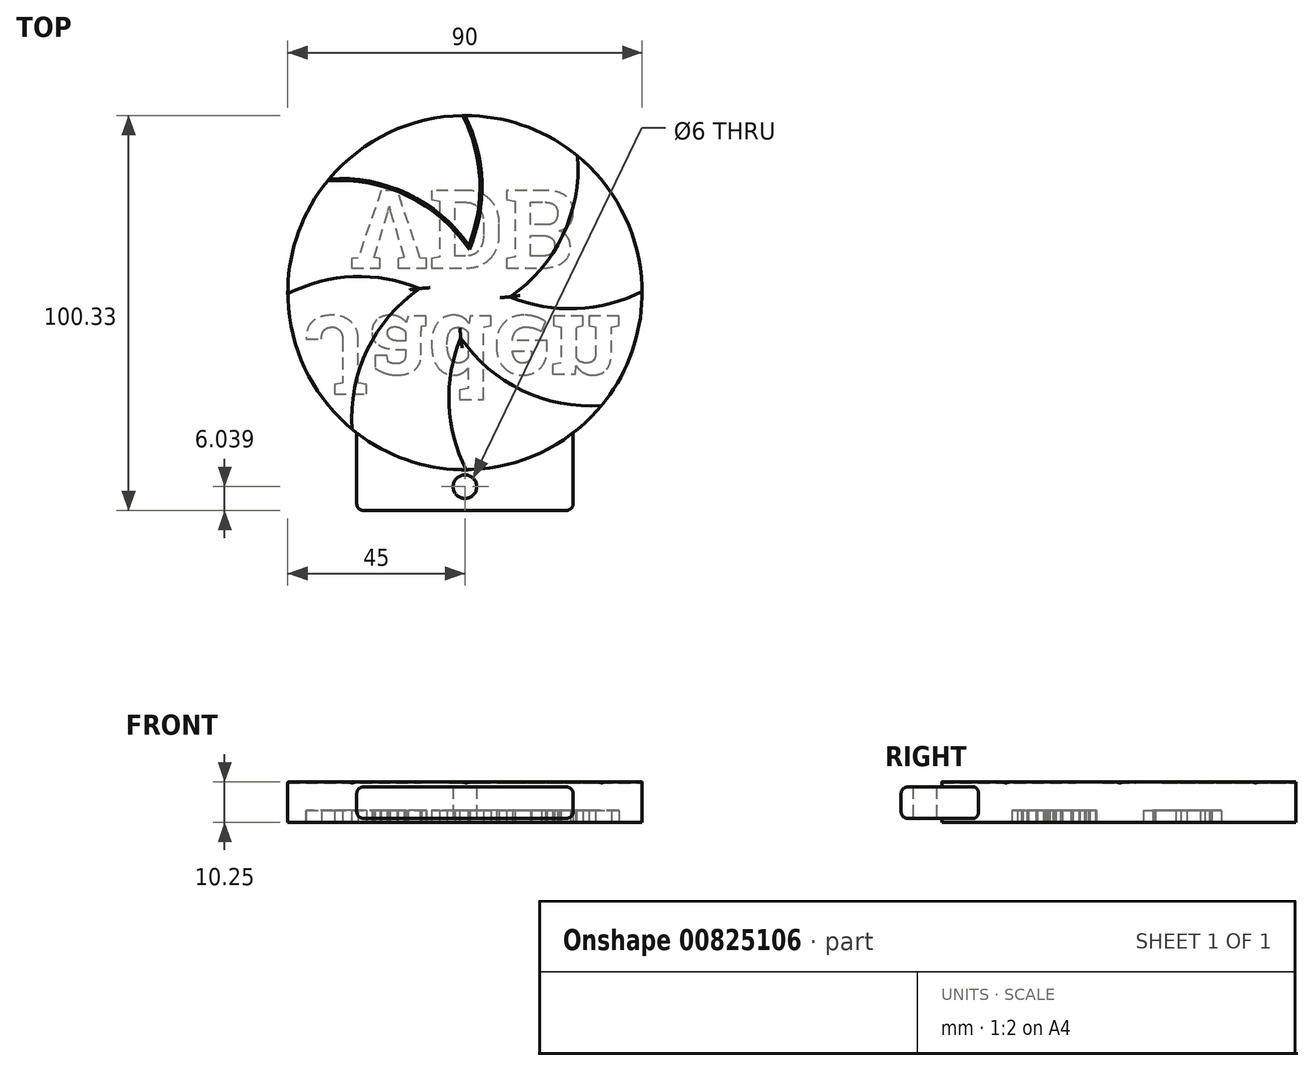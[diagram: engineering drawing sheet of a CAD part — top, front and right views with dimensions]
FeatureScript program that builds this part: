
annotation { "Feature Type Name" : "Feature", "Feature Type Description" : "" }
export const myFeature = defineFeature(function(context is Context, id is Id, definition is map)
    precondition{}
    {
        {
            var Q0;
            Q0=qCreatedBy(makeId("Top.planeOp"),FACE);
            var sketch = newSketch(context, id + "F0", { "sketchPlane" : qUnion([Q0])});
            skPoint(sketch, "E0.middle", {"position": v(0, 0) * mm});
            skCircle(sketch, "E1", {"center": v(0, 0) * mm, "radius": 45 * mm});
            skSolve(sketch);
        }
        {
            var Q0;
            Q0 = qSketchRegion(id + "F0", true);
            extrude(context, id + "F1", {"entities" : qUnion([Q0]), "endBound" : BoundingType.SYMMETRIC, "depth" : 10 * mm, "offsetDistance" : 25 * mm});
        }
        {
            var Q0;
            Q0=qCreatedBy(makeId("Top.planeOp"),FACE);
            var sketch = newSketch(context, id + "F2", { "sketchPlane" : qUnion([Q0])});
            skCircle(sketch, "E2.0", {"center": v(0, 0) * mm, "radius": 45 * mm});
            skLineSegment(sketch, "E3", {"start": v(-27.5, -35.62) * mm, "end": v(-27.5, -55.33) * mm});
            skLineSegment(sketch, "E4", {"start": v(-27.5, -55.33) * mm, "end": v(27.5, -55.33) * mm});
            skLineSegment(sketch, "E5", {"start": v(27.5, -55.33) * mm, "end": v(27.5, -35.62) * mm});
            skSolve(sketch);
        }
        {
            var Q0;
            Q0 = qSketchRegion(id + "F2", true);
            extrude(context, id + "F3", {"entities" : qUnion([Q0]), "operationType" : NewBodyOperationType.ADD, "endBound" : BoundingType.SYMMETRIC, "depth" : 8 * mm, "offsetDistance" : 25 * mm});
        }
        {
            var Q0;
            Q0=makeQuery(id+"F1.opExtrude","CAP_FACE",FACE,{"disambiguationData":[OSD([sQuery(id+"F0.wireOp",EDGE,"E1")])],"isStart":false});
            var sketch = newSketch(context, id + "F4", { "sketchPlane" : qUnion([Q0])});
            skArc(sketch, "E6", {"start": v(1, 12) * mm, "mid": v(-14.52, 25.11) * mm, "end": v(-34.48, 28.92) * mm});
            skArc(sketch, "E7", {"start": v(1, 12) * mm, "mid": v(3.78, 28.66) * mm, "end": v(-0.56, 45) * mm});
            skPoint(sketch, "E8.center", {"position": v(0, 0) * mm});
            skArc(sketch, "E9.0", {"start": v(-0.56, 45) * mm, "mid": v(-19.27, 40.66) * mm, "end": v(-34.48, 28.92) * mm});
            skArc(sketch, "E10.0", {"start": v(1.1, 10.95) * mm, "mid": v(4.3, 28.1) * mm, "end": v(0, 45) * mm});
            skArc(sketch, "E10.1", {"start": v(1.1, 10.95) * mm, "mid": v(-14.53, 24.57) * mm, "end": v(-34.92, 28.39) * mm});
            skArc(sketch, "E11.1.0", {"start": v(-10.95, 1.1) * mm, "mid": v(-28.1, 4.3) * mm, "end": v(-45, 0) * mm});
            skArc(sketch, "E11.1.1", {"start": v(-12, 1) * mm, "mid": v(-28.66, 3.78) * mm, "end": v(-45, -0.56) * mm});
            skArc(sketch, "E11.1.2", {"start": v(-12, 1) * mm, "mid": v(-25.11, -14.52) * mm, "end": v(-28.92, -34.48) * mm});
            skArc(sketch, "E11.1.3", {"start": v(-10.95, 1.1) * mm, "mid": v(-24.57, -14.53) * mm, "end": v(-28.39, -34.92) * mm});
            skArc(sketch, "E11.2.0", {"start": v(-1.1, -10.95) * mm, "mid": v(-4.3, -28.1) * mm, "end": v(0, -45) * mm});
            skArc(sketch, "E11.2.1", {"start": v(-1, -12) * mm, "mid": v(-3.78, -28.66) * mm, "end": v(0.56, -45) * mm});
            skArc(sketch, "E11.2.2", {"start": v(-1, -12) * mm, "mid": v(14.52, -25.11) * mm, "end": v(34.48, -28.92) * mm});
            skArc(sketch, "E11.2.3", {"start": v(-1.1, -10.95) * mm, "mid": v(14.53, -24.57) * mm, "end": v(34.92, -28.39) * mm});
            skArc(sketch, "E11.3.0", {"start": v(10.95, -1.1) * mm, "mid": v(28.1, -4.3) * mm, "end": v(45, 0) * mm});
            skArc(sketch, "E11.3.1", {"start": v(12, -1) * mm, "mid": v(28.66, -3.78) * mm, "end": v(45, 0.56) * mm});
            skArc(sketch, "E11.3.2", {"start": v(12, -1) * mm, "mid": v(25.11, 14.52) * mm, "end": v(28.92, 34.48) * mm});
            skArc(sketch, "E11.3.3", {"start": v(10.95, -1.1) * mm, "mid": v(24.57, 14.53) * mm, "end": v(28.39, 34.92) * mm});
            skArc(sketch, "E12.trimOffspring", {"start": v(-34.92, 28.39) * mm, "mid": v(-42.4, 15.06) * mm, "end": v(-45, 0) * mm});
            skArc(sketch, "E13.trimOffspring", {"start": v(-45, -0.56) * mm, "mid": v(-40.66, -19.27) * mm, "end": v(-28.92, -34.48) * mm});
            skArc(sketch, "E14.trimOffspring", {"start": v(-28.39, -34.92) * mm, "mid": v(-15.06, -42.4) * mm, "end": v(0, -45) * mm});
            skArc(sketch, "E15.trimOffspring", {"start": v(0.56, -45) * mm, "mid": v(19.27, -40.66) * mm, "end": v(34.48, -28.92) * mm});
            skArc(sketch, "E16.trimOffspring", {"start": v(34.92, -28.39) * mm, "mid": v(42.4, -15.06) * mm, "end": v(45, 0) * mm});
            skArc(sketch, "E17.trimOffspring", {"start": v(45, 0.56) * mm, "mid": v(40.66, 19.27) * mm, "end": v(28.92, 34.48) * mm});
            skArc(sketch, "E18.trimOffspring", {"start": v(28.39, 34.92) * mm, "mid": v(15.06, 42.4) * mm, "end": v(0, 45) * mm});
            skSolve(sketch);
        }
        {
            var Q0;
            Q0 = qSketchRegion(id + "F4", true);
            extrude(context, id + "F5", {"entities" : qUnion([Q0]), "operationType" : NewBodyOperationType.ADD, "depth" : .25 * mm, "offsetDistance" : 25 * mm});
        }
        {
            var Q0;
            Q0=makeQuery(id+"F5.opExtrude","CAP_EDGE",EDGE,{"disambiguationData":[OSD([sQuery(id+"F4.wireOp",EDGE,"E11.1.2")])],"isStart":true});
            var Q1;
            Q1=makeQuery(id+"F5.opExtrude","CAP_EDGE",EDGE,{"disambiguationData":[OSD([sQuery(id+"F4.wireOp",EDGE,"E11.1.3")])],"isStart":true});
            var Q2;
            Q2=makeQuery(id+"F5.opExtrude","CAP_EDGE",EDGE,{"disambiguationData":[OSD([sQuery(id+"F4.wireOp",EDGE,"E11.1.0")])],"isStart":true});
            var Q3;
            Q3=makeQuery(id+"F5.opExtrude","CAP_EDGE",EDGE,{"disambiguationData":[OSD([sQuery(id+"F4.wireOp",EDGE,"E11.1.1")])],"isStart":true});
            var Q4;
            Q4=makeQuery(id+"F5.opExtrude","CAP_EDGE",EDGE,{"disambiguationData":[OSD([sQuery(id+"F4.wireOp",EDGE,"E6")])],"isStart":true});
            var Q5;
            Q5=makeQuery(id+"F5.opExtrude","CAP_EDGE",EDGE,{"disambiguationData":[OSD([sQuery(id+"F4.wireOp",EDGE,"E10.1")])],"isStart":true});
            var Q6;
            Q6=makeQuery(id+"F5.opExtrude","CAP_EDGE",EDGE,{"disambiguationData":[OSD([sQuery(id+"F4.wireOp",EDGE,"E7")])],"isStart":true});
            var Q7;
            Q7=makeQuery(id+"F5.opExtrude","CAP_EDGE",EDGE,{"disambiguationData":[OSD([sQuery(id+"F4.wireOp",EDGE,"E10.0")])],"isStart":true});
            var Q8;
            Q8=makeQuery(id+"F5.opExtrude","CAP_EDGE",EDGE,{"disambiguationData":[OSD([sQuery(id+"F4.wireOp",EDGE,"E11.3.2")])],"isStart":true});
            var Q9;
            Q9=makeQuery(id+"F5.opExtrude","CAP_EDGE",EDGE,{"disambiguationData":[OSD([sQuery(id+"F4.wireOp",EDGE,"E11.3.3")])],"isStart":true});
            var Q10;
            Q10=makeQuery(id+"F5.opExtrude","CAP_EDGE",EDGE,{"disambiguationData":[OSD([sQuery(id+"F4.wireOp",EDGE,"E11.3.1")])],"isStart":true});
            var Q11;
            Q11=makeQuery(id+"F5.opExtrude","CAP_EDGE",EDGE,{"disambiguationData":[OSD([sQuery(id+"F4.wireOp",EDGE,"E11.3.0")])],"isStart":true});
            var Q12;
            Q12=makeQuery(id+"F5.opExtrude","CAP_EDGE",EDGE,{"disambiguationData":[OSD([sQuery(id+"F4.wireOp",EDGE,"E11.2.2")])],"isStart":true});
            var Q13;
            Q13=makeQuery(id+"F5.opExtrude","CAP_EDGE",EDGE,{"disambiguationData":[OSD([sQuery(id+"F4.wireOp",EDGE,"E11.2.3")])],"isStart":true});
            var Q14;
            Q14=makeQuery(id+"F5.opExtrude","CAP_EDGE",EDGE,{"disambiguationData":[OSD([sQuery(id+"F4.wireOp",EDGE,"E11.2.0")])],"isStart":true});
            var Q15;
            Q15=makeQuery(id+"F5.opExtrude","CAP_EDGE",EDGE,{"disambiguationData":[OSD([sQuery(id+"F4.wireOp",EDGE,"E11.2.1")])],"isStart":true});
            fillet(context, id + "F6", {"entities" : qUnion([Q0, Q1, Q2, Q3, Q4, Q5, Q6, Q7, Q8, Q9, Q10, Q11, Q12, Q13, Q14, Q15]), "radius" : .3 * mm, "tangentPropagation" : true, "allowEdgeOverflow" : false});
        }
        {
            var Q0;
            {var subQ0=sQuery(id+"F4.wireOp",EDGE,"E7");Q0=makeQuery(id+"F6.opFillet","BLEND_EDGE",EDGE,{"blendedFrom":[makeQuery(id+"F5.opExtrude","CAP_EDGE",EDGE,{"disambiguationData":[OSD([subQ0])],"isStart":true}),makeQuery(id+"F5.opExtrude","CAP_FACE",FACE,{"disambiguationData":[OSD([sQuery(id+"F4.wireOp",EDGE,"E6"),subQ0,sQuery(id+"F4.wireOp",EDGE,"E9.0")])],"isStart":false})],"blendedInto":[makeQuery(id+"F5.opExtrude","CAP_FACE",FACE,{"disambiguationData":[OSD([sQuery(id+"F4.wireOp",EDGE,"E6"),subQ0,sQuery(id+"F4.wireOp",EDGE,"E9.0")])],"isStart":false})]});}
            var Q1;
            {var subQ0=sQuery(id+"F4.wireOp",EDGE,"E10.0");Q1=makeQuery(id+"F6.opFillet","BLEND_EDGE",EDGE,{"blendedFrom":[makeQuery(id+"F5.opExtrude","CAP_EDGE",EDGE,{"disambiguationData":[OSD([subQ0])],"isStart":true}),makeQuery(id+"F5.opExtrude","CAP_FACE",FACE,{"disambiguationData":[OSD([subQ0,sQuery(id+"F4.wireOp",EDGE,"E10.1"),sQuery(id+"F4.wireOp",EDGE,"E11.1.0"),sQuery(id+"F4.wireOp",EDGE,"E11.1.3"),sQuery(id+"F4.wireOp",EDGE,"E11.2.0"),sQuery(id+"F4.wireOp",EDGE,"E11.2.3"),sQuery(id+"F4.wireOp",EDGE,"E11.3.0"),sQuery(id+"F4.wireOp",EDGE,"E11.3.3"),sQuery(id+"F4.wireOp",EDGE,"E12.trimOffspring"),sQuery(id+"F4.wireOp",EDGE,"E14.trimOffspring"),sQuery(id+"F4.wireOp",EDGE,"E16.trimOffspring"),sQuery(id+"F4.wireOp",EDGE,"E18.trimOffspring")])],"isStart":false})],"blendedInto":[makeQuery(id+"F5.opExtrude","CAP_FACE",FACE,{"disambiguationData":[OSD([subQ0,sQuery(id+"F4.wireOp",EDGE,"E10.1"),sQuery(id+"F4.wireOp",EDGE,"E11.1.0"),sQuery(id+"F4.wireOp",EDGE,"E11.1.3"),sQuery(id+"F4.wireOp",EDGE,"E11.2.0"),sQuery(id+"F4.wireOp",EDGE,"E11.2.3"),sQuery(id+"F4.wireOp",EDGE,"E11.3.0"),sQuery(id+"F4.wireOp",EDGE,"E11.3.3"),sQuery(id+"F4.wireOp",EDGE,"E12.trimOffspring"),sQuery(id+"F4.wireOp",EDGE,"E14.trimOffspring"),sQuery(id+"F4.wireOp",EDGE,"E16.trimOffspring"),sQuery(id+"F4.wireOp",EDGE,"E18.trimOffspring")])],"isStart":false})]});}
            var Q2;
            {var subQ0=sQuery(id+"F4.wireOp",EDGE,"E6");Q2=makeQuery(id+"F6.opFillet","BLEND_EDGE",EDGE,{"blendedFrom":[makeQuery(id+"F5.opExtrude","CAP_EDGE",EDGE,{"disambiguationData":[OSD([subQ0])],"isStart":true}),makeQuery(id+"F5.opExtrude","CAP_FACE",FACE,{"disambiguationData":[OSD([subQ0,sQuery(id+"F4.wireOp",EDGE,"E7"),sQuery(id+"F4.wireOp",EDGE,"E9.0")])],"isStart":false})],"blendedInto":[makeQuery(id+"F5.opExtrude","CAP_FACE",FACE,{"disambiguationData":[OSD([subQ0,sQuery(id+"F4.wireOp",EDGE,"E7"),sQuery(id+"F4.wireOp",EDGE,"E9.0")])],"isStart":false})]});}
            var Q3;
            {var subQ0=sQuery(id+"F4.wireOp",EDGE,"E10.1");Q3=makeQuery(id+"F6.opFillet","BLEND_EDGE",EDGE,{"blendedFrom":[makeQuery(id+"F5.opExtrude","CAP_EDGE",EDGE,{"disambiguationData":[OSD([subQ0])],"isStart":true}),makeQuery(id+"F5.opExtrude","CAP_FACE",FACE,{"disambiguationData":[OSD([sQuery(id+"F4.wireOp",EDGE,"E10.0"),subQ0,sQuery(id+"F4.wireOp",EDGE,"E11.1.0"),sQuery(id+"F4.wireOp",EDGE,"E11.1.3"),sQuery(id+"F4.wireOp",EDGE,"E11.2.0"),sQuery(id+"F4.wireOp",EDGE,"E11.2.3"),sQuery(id+"F4.wireOp",EDGE,"E11.3.0"),sQuery(id+"F4.wireOp",EDGE,"E11.3.3"),sQuery(id+"F4.wireOp",EDGE,"E12.trimOffspring"),sQuery(id+"F4.wireOp",EDGE,"E14.trimOffspring"),sQuery(id+"F4.wireOp",EDGE,"E16.trimOffspring"),sQuery(id+"F4.wireOp",EDGE,"E18.trimOffspring")])],"isStart":false})],"blendedInto":[makeQuery(id+"F5.opExtrude","CAP_FACE",FACE,{"disambiguationData":[OSD([sQuery(id+"F4.wireOp",EDGE,"E10.0"),subQ0,sQuery(id+"F4.wireOp",EDGE,"E11.1.0"),sQuery(id+"F4.wireOp",EDGE,"E11.1.3"),sQuery(id+"F4.wireOp",EDGE,"E11.2.0"),sQuery(id+"F4.wireOp",EDGE,"E11.2.3"),sQuery(id+"F4.wireOp",EDGE,"E11.3.0"),sQuery(id+"F4.wireOp",EDGE,"E11.3.3"),sQuery(id+"F4.wireOp",EDGE,"E12.trimOffspring"),sQuery(id+"F4.wireOp",EDGE,"E14.trimOffspring"),sQuery(id+"F4.wireOp",EDGE,"E16.trimOffspring"),sQuery(id+"F4.wireOp",EDGE,"E18.trimOffspring")])],"isStart":false})]});}
            var Q4;
            {var subQ0=sQuery(id+"F4.wireOp",EDGE,"E11.3.3");Q4=makeQuery(id+"F6.opFillet","BLEND_EDGE",EDGE,{"blendedFrom":[makeQuery(id+"F5.opExtrude","CAP_EDGE",EDGE,{"disambiguationData":[OSD([subQ0])],"isStart":true}),makeQuery(id+"F5.opExtrude","CAP_FACE",FACE,{"disambiguationData":[OSD([sQuery(id+"F4.wireOp",EDGE,"E10.0"),sQuery(id+"F4.wireOp",EDGE,"E10.1"),sQuery(id+"F4.wireOp",EDGE,"E11.1.0"),sQuery(id+"F4.wireOp",EDGE,"E11.1.3"),sQuery(id+"F4.wireOp",EDGE,"E11.2.0"),sQuery(id+"F4.wireOp",EDGE,"E11.2.3"),sQuery(id+"F4.wireOp",EDGE,"E11.3.0"),subQ0,sQuery(id+"F4.wireOp",EDGE,"E12.trimOffspring"),sQuery(id+"F4.wireOp",EDGE,"E14.trimOffspring"),sQuery(id+"F4.wireOp",EDGE,"E16.trimOffspring"),sQuery(id+"F4.wireOp",EDGE,"E18.trimOffspring")])],"isStart":false})],"blendedInto":[makeQuery(id+"F5.opExtrude","CAP_FACE",FACE,{"disambiguationData":[OSD([sQuery(id+"F4.wireOp",EDGE,"E10.0"),sQuery(id+"F4.wireOp",EDGE,"E10.1"),sQuery(id+"F4.wireOp",EDGE,"E11.1.0"),sQuery(id+"F4.wireOp",EDGE,"E11.1.3"),sQuery(id+"F4.wireOp",EDGE,"E11.2.0"),sQuery(id+"F4.wireOp",EDGE,"E11.2.3"),sQuery(id+"F4.wireOp",EDGE,"E11.3.0"),subQ0,sQuery(id+"F4.wireOp",EDGE,"E12.trimOffspring"),sQuery(id+"F4.wireOp",EDGE,"E14.trimOffspring"),sQuery(id+"F4.wireOp",EDGE,"E16.trimOffspring"),sQuery(id+"F4.wireOp",EDGE,"E18.trimOffspring")])],"isStart":false})]});}
            var Q5;
            {var subQ0=sQuery(id+"F4.wireOp",EDGE,"E11.3.2");Q5=makeQuery(id+"F6.opFillet","BLEND_EDGE",EDGE,{"blendedFrom":[makeQuery(id+"F5.opExtrude","CAP_EDGE",EDGE,{"disambiguationData":[OSD([subQ0])],"isStart":true}),makeQuery(id+"F5.opExtrude","CAP_FACE",FACE,{"disambiguationData":[OSD([sQuery(id+"F4.wireOp",EDGE,"E11.3.1"),subQ0,sQuery(id+"F4.wireOp",EDGE,"E17.trimOffspring")])],"isStart":false})],"blendedInto":[makeQuery(id+"F5.opExtrude","CAP_FACE",FACE,{"disambiguationData":[OSD([sQuery(id+"F4.wireOp",EDGE,"E11.3.1"),subQ0,sQuery(id+"F4.wireOp",EDGE,"E17.trimOffspring")])],"isStart":false})]});}
            var Q6;
            {var subQ0=sQuery(id+"F4.wireOp",EDGE,"E11.3.1");Q6=makeQuery(id+"F6.opFillet","BLEND_EDGE",EDGE,{"blendedFrom":[makeQuery(id+"F5.opExtrude","CAP_EDGE",EDGE,{"disambiguationData":[OSD([subQ0])],"isStart":true}),makeQuery(id+"F5.opExtrude","CAP_FACE",FACE,{"disambiguationData":[OSD([subQ0,sQuery(id+"F4.wireOp",EDGE,"E11.3.2"),sQuery(id+"F4.wireOp",EDGE,"E17.trimOffspring")])],"isStart":false})],"blendedInto":[makeQuery(id+"F5.opExtrude","CAP_FACE",FACE,{"disambiguationData":[OSD([subQ0,sQuery(id+"F4.wireOp",EDGE,"E11.3.2"),sQuery(id+"F4.wireOp",EDGE,"E17.trimOffspring")])],"isStart":false})]});}
            var Q7;
            {var subQ0=sQuery(id+"F4.wireOp",EDGE,"E11.3.0");Q7=makeQuery(id+"F6.opFillet","BLEND_EDGE",EDGE,{"blendedFrom":[makeQuery(id+"F5.opExtrude","CAP_EDGE",EDGE,{"disambiguationData":[OSD([subQ0])],"isStart":true}),makeQuery(id+"F5.opExtrude","CAP_FACE",FACE,{"disambiguationData":[OSD([sQuery(id+"F4.wireOp",EDGE,"E10.0"),sQuery(id+"F4.wireOp",EDGE,"E10.1"),sQuery(id+"F4.wireOp",EDGE,"E11.1.0"),sQuery(id+"F4.wireOp",EDGE,"E11.1.3"),sQuery(id+"F4.wireOp",EDGE,"E11.2.0"),sQuery(id+"F4.wireOp",EDGE,"E11.2.3"),subQ0,sQuery(id+"F4.wireOp",EDGE,"E11.3.3"),sQuery(id+"F4.wireOp",EDGE,"E12.trimOffspring"),sQuery(id+"F4.wireOp",EDGE,"E14.trimOffspring"),sQuery(id+"F4.wireOp",EDGE,"E16.trimOffspring"),sQuery(id+"F4.wireOp",EDGE,"E18.trimOffspring")])],"isStart":false})],"blendedInto":[makeQuery(id+"F5.opExtrude","CAP_FACE",FACE,{"disambiguationData":[OSD([sQuery(id+"F4.wireOp",EDGE,"E10.0"),sQuery(id+"F4.wireOp",EDGE,"E10.1"),sQuery(id+"F4.wireOp",EDGE,"E11.1.0"),sQuery(id+"F4.wireOp",EDGE,"E11.1.3"),sQuery(id+"F4.wireOp",EDGE,"E11.2.0"),sQuery(id+"F4.wireOp",EDGE,"E11.2.3"),subQ0,sQuery(id+"F4.wireOp",EDGE,"E11.3.3"),sQuery(id+"F4.wireOp",EDGE,"E12.trimOffspring"),sQuery(id+"F4.wireOp",EDGE,"E14.trimOffspring"),sQuery(id+"F4.wireOp",EDGE,"E16.trimOffspring"),sQuery(id+"F4.wireOp",EDGE,"E18.trimOffspring")])],"isStart":false})]});}
            var Q8;
            {var subQ0=sQuery(id+"F4.wireOp",EDGE,"E11.2.3");Q8=makeQuery(id+"F6.opFillet","BLEND_EDGE",EDGE,{"blendedFrom":[makeQuery(id+"F5.opExtrude","CAP_EDGE",EDGE,{"disambiguationData":[OSD([subQ0])],"isStart":true}),makeQuery(id+"F5.opExtrude","CAP_FACE",FACE,{"disambiguationData":[OSD([sQuery(id+"F4.wireOp",EDGE,"E10.0"),sQuery(id+"F4.wireOp",EDGE,"E10.1"),sQuery(id+"F4.wireOp",EDGE,"E11.1.0"),sQuery(id+"F4.wireOp",EDGE,"E11.1.3"),sQuery(id+"F4.wireOp",EDGE,"E11.2.0"),subQ0,sQuery(id+"F4.wireOp",EDGE,"E11.3.0"),sQuery(id+"F4.wireOp",EDGE,"E11.3.3"),sQuery(id+"F4.wireOp",EDGE,"E12.trimOffspring"),sQuery(id+"F4.wireOp",EDGE,"E14.trimOffspring"),sQuery(id+"F4.wireOp",EDGE,"E16.trimOffspring"),sQuery(id+"F4.wireOp",EDGE,"E18.trimOffspring")])],"isStart":false})],"blendedInto":[makeQuery(id+"F5.opExtrude","CAP_FACE",FACE,{"disambiguationData":[OSD([sQuery(id+"F4.wireOp",EDGE,"E10.0"),sQuery(id+"F4.wireOp",EDGE,"E10.1"),sQuery(id+"F4.wireOp",EDGE,"E11.1.0"),sQuery(id+"F4.wireOp",EDGE,"E11.1.3"),sQuery(id+"F4.wireOp",EDGE,"E11.2.0"),subQ0,sQuery(id+"F4.wireOp",EDGE,"E11.3.0"),sQuery(id+"F4.wireOp",EDGE,"E11.3.3"),sQuery(id+"F4.wireOp",EDGE,"E12.trimOffspring"),sQuery(id+"F4.wireOp",EDGE,"E14.trimOffspring"),sQuery(id+"F4.wireOp",EDGE,"E16.trimOffspring"),sQuery(id+"F4.wireOp",EDGE,"E18.trimOffspring")])],"isStart":false})]});}
            var Q9;
            {var subQ0=sQuery(id+"F4.wireOp",EDGE,"E11.2.2");Q9=makeQuery(id+"F6.opFillet","BLEND_EDGE",EDGE,{"blendedFrom":[makeQuery(id+"F5.opExtrude","CAP_EDGE",EDGE,{"disambiguationData":[OSD([subQ0])],"isStart":true}),makeQuery(id+"F5.opExtrude","CAP_FACE",FACE,{"disambiguationData":[OSD([sQuery(id+"F4.wireOp",EDGE,"E11.2.1"),subQ0,sQuery(id+"F4.wireOp",EDGE,"E15.trimOffspring")])],"isStart":false})],"blendedInto":[makeQuery(id+"F5.opExtrude","CAP_FACE",FACE,{"disambiguationData":[OSD([sQuery(id+"F4.wireOp",EDGE,"E11.2.1"),subQ0,sQuery(id+"F4.wireOp",EDGE,"E15.trimOffspring")])],"isStart":false})]});}
            var Q10;
            {var subQ0=sQuery(id+"F4.wireOp",EDGE,"E11.2.1");Q10=makeQuery(id+"F6.opFillet","BLEND_EDGE",EDGE,{"blendedFrom":[makeQuery(id+"F5.opExtrude","CAP_EDGE",EDGE,{"disambiguationData":[OSD([subQ0])],"isStart":true}),makeQuery(id+"F5.opExtrude","CAP_FACE",FACE,{"disambiguationData":[OSD([subQ0,sQuery(id+"F4.wireOp",EDGE,"E11.2.2"),sQuery(id+"F4.wireOp",EDGE,"E15.trimOffspring")])],"isStart":false})],"blendedInto":[makeQuery(id+"F5.opExtrude","CAP_FACE",FACE,{"disambiguationData":[OSD([subQ0,sQuery(id+"F4.wireOp",EDGE,"E11.2.2"),sQuery(id+"F4.wireOp",EDGE,"E15.trimOffspring")])],"isStart":false})]});}
            var Q11;
            {var subQ0=sQuery(id+"F4.wireOp",EDGE,"E11.2.0");Q11=makeQuery(id+"F6.opFillet","BLEND_EDGE",EDGE,{"blendedFrom":[makeQuery(id+"F5.opExtrude","CAP_EDGE",EDGE,{"disambiguationData":[OSD([subQ0])],"isStart":true}),makeQuery(id+"F5.opExtrude","CAP_FACE",FACE,{"disambiguationData":[OSD([sQuery(id+"F4.wireOp",EDGE,"E10.0"),sQuery(id+"F4.wireOp",EDGE,"E10.1"),sQuery(id+"F4.wireOp",EDGE,"E11.1.0"),sQuery(id+"F4.wireOp",EDGE,"E11.1.3"),subQ0,sQuery(id+"F4.wireOp",EDGE,"E11.2.3"),sQuery(id+"F4.wireOp",EDGE,"E11.3.0"),sQuery(id+"F4.wireOp",EDGE,"E11.3.3"),sQuery(id+"F4.wireOp",EDGE,"E12.trimOffspring"),sQuery(id+"F4.wireOp",EDGE,"E14.trimOffspring"),sQuery(id+"F4.wireOp",EDGE,"E16.trimOffspring"),sQuery(id+"F4.wireOp",EDGE,"E18.trimOffspring")])],"isStart":false})],"blendedInto":[makeQuery(id+"F5.opExtrude","CAP_FACE",FACE,{"disambiguationData":[OSD([sQuery(id+"F4.wireOp",EDGE,"E10.0"),sQuery(id+"F4.wireOp",EDGE,"E10.1"),sQuery(id+"F4.wireOp",EDGE,"E11.1.0"),sQuery(id+"F4.wireOp",EDGE,"E11.1.3"),subQ0,sQuery(id+"F4.wireOp",EDGE,"E11.2.3"),sQuery(id+"F4.wireOp",EDGE,"E11.3.0"),sQuery(id+"F4.wireOp",EDGE,"E11.3.3"),sQuery(id+"F4.wireOp",EDGE,"E12.trimOffspring"),sQuery(id+"F4.wireOp",EDGE,"E14.trimOffspring"),sQuery(id+"F4.wireOp",EDGE,"E16.trimOffspring"),sQuery(id+"F4.wireOp",EDGE,"E18.trimOffspring")])],"isStart":false})]});}
            var Q12;
            {var subQ0=sQuery(id+"F4.wireOp",EDGE,"E11.1.0");Q12=makeQuery(id+"F6.opFillet","BLEND_EDGE",EDGE,{"blendedFrom":[makeQuery(id+"F5.opExtrude","CAP_EDGE",EDGE,{"disambiguationData":[OSD([subQ0])],"isStart":true}),makeQuery(id+"F5.opExtrude","CAP_FACE",FACE,{"disambiguationData":[OSD([sQuery(id+"F4.wireOp",EDGE,"E10.0"),sQuery(id+"F4.wireOp",EDGE,"E10.1"),subQ0,sQuery(id+"F4.wireOp",EDGE,"E11.1.3"),sQuery(id+"F4.wireOp",EDGE,"E11.2.0"),sQuery(id+"F4.wireOp",EDGE,"E11.2.3"),sQuery(id+"F4.wireOp",EDGE,"E11.3.0"),sQuery(id+"F4.wireOp",EDGE,"E11.3.3"),sQuery(id+"F4.wireOp",EDGE,"E12.trimOffspring"),sQuery(id+"F4.wireOp",EDGE,"E14.trimOffspring"),sQuery(id+"F4.wireOp",EDGE,"E16.trimOffspring"),sQuery(id+"F4.wireOp",EDGE,"E18.trimOffspring")])],"isStart":false})],"blendedInto":[makeQuery(id+"F5.opExtrude","CAP_FACE",FACE,{"disambiguationData":[OSD([sQuery(id+"F4.wireOp",EDGE,"E10.0"),sQuery(id+"F4.wireOp",EDGE,"E10.1"),subQ0,sQuery(id+"F4.wireOp",EDGE,"E11.1.3"),sQuery(id+"F4.wireOp",EDGE,"E11.2.0"),sQuery(id+"F4.wireOp",EDGE,"E11.2.3"),sQuery(id+"F4.wireOp",EDGE,"E11.3.0"),sQuery(id+"F4.wireOp",EDGE,"E11.3.3"),sQuery(id+"F4.wireOp",EDGE,"E12.trimOffspring"),sQuery(id+"F4.wireOp",EDGE,"E14.trimOffspring"),sQuery(id+"F4.wireOp",EDGE,"E16.trimOffspring"),sQuery(id+"F4.wireOp",EDGE,"E18.trimOffspring")])],"isStart":false})]});}
            var Q13;
            {var subQ0=sQuery(id+"F4.wireOp",EDGE,"E11.1.1");Q13=makeQuery(id+"F6.opFillet","BLEND_EDGE",EDGE,{"blendedFrom":[makeQuery(id+"F5.opExtrude","CAP_EDGE",EDGE,{"disambiguationData":[OSD([subQ0])],"isStart":true}),makeQuery(id+"F5.opExtrude","CAP_FACE",FACE,{"disambiguationData":[OSD([subQ0,sQuery(id+"F4.wireOp",EDGE,"E11.1.2"),sQuery(id+"F4.wireOp",EDGE,"E13.trimOffspring")])],"isStart":false})],"blendedInto":[makeQuery(id+"F5.opExtrude","CAP_FACE",FACE,{"disambiguationData":[OSD([subQ0,sQuery(id+"F4.wireOp",EDGE,"E11.1.2"),sQuery(id+"F4.wireOp",EDGE,"E13.trimOffspring")])],"isStart":false})]});}
            var Q14;
            {var subQ0=sQuery(id+"F4.wireOp",EDGE,"E11.1.2");Q14=makeQuery(id+"F6.opFillet","BLEND_EDGE",EDGE,{"blendedFrom":[makeQuery(id+"F5.opExtrude","CAP_EDGE",EDGE,{"disambiguationData":[OSD([subQ0])],"isStart":true}),makeQuery(id+"F5.opExtrude","CAP_FACE",FACE,{"disambiguationData":[OSD([sQuery(id+"F4.wireOp",EDGE,"E11.1.1"),subQ0,sQuery(id+"F4.wireOp",EDGE,"E13.trimOffspring")])],"isStart":false})],"blendedInto":[makeQuery(id+"F5.opExtrude","CAP_FACE",FACE,{"disambiguationData":[OSD([sQuery(id+"F4.wireOp",EDGE,"E11.1.1"),subQ0,sQuery(id+"F4.wireOp",EDGE,"E13.trimOffspring")])],"isStart":false})]});}
            var Q15;
            {var subQ0=sQuery(id+"F4.wireOp",EDGE,"E11.1.3");Q15=makeQuery(id+"F6.opFillet","BLEND_EDGE",EDGE,{"blendedFrom":[makeQuery(id+"F5.opExtrude","CAP_EDGE",EDGE,{"disambiguationData":[OSD([subQ0])],"isStart":true}),makeQuery(id+"F5.opExtrude","CAP_FACE",FACE,{"disambiguationData":[OSD([sQuery(id+"F4.wireOp",EDGE,"E10.0"),sQuery(id+"F4.wireOp",EDGE,"E10.1"),sQuery(id+"F4.wireOp",EDGE,"E11.1.0"),subQ0,sQuery(id+"F4.wireOp",EDGE,"E11.2.0"),sQuery(id+"F4.wireOp",EDGE,"E11.2.3"),sQuery(id+"F4.wireOp",EDGE,"E11.3.0"),sQuery(id+"F4.wireOp",EDGE,"E11.3.3"),sQuery(id+"F4.wireOp",EDGE,"E12.trimOffspring"),sQuery(id+"F4.wireOp",EDGE,"E14.trimOffspring"),sQuery(id+"F4.wireOp",EDGE,"E16.trimOffspring"),sQuery(id+"F4.wireOp",EDGE,"E18.trimOffspring")])],"isStart":false})],"blendedInto":[makeQuery(id+"F5.opExtrude","CAP_FACE",FACE,{"disambiguationData":[OSD([sQuery(id+"F4.wireOp",EDGE,"E10.0"),sQuery(id+"F4.wireOp",EDGE,"E10.1"),sQuery(id+"F4.wireOp",EDGE,"E11.1.0"),subQ0,sQuery(id+"F4.wireOp",EDGE,"E11.2.0"),sQuery(id+"F4.wireOp",EDGE,"E11.2.3"),sQuery(id+"F4.wireOp",EDGE,"E11.3.0"),sQuery(id+"F4.wireOp",EDGE,"E11.3.3"),sQuery(id+"F4.wireOp",EDGE,"E12.trimOffspring"),sQuery(id+"F4.wireOp",EDGE,"E14.trimOffspring"),sQuery(id+"F4.wireOp",EDGE,"E16.trimOffspring"),sQuery(id+"F4.wireOp",EDGE,"E18.trimOffspring")])],"isStart":false})]});}
            fillet(context, id + "F7", {"entities" : qUnion([Q0, Q1, Q2, Q3, Q4, Q5, Q6, Q7, Q8, Q9, Q10, Q11, Q12, Q13, Q14, Q15]), "radius" : 3 * mm, "tangentPropagation" : true, "allowEdgeOverflow" : false});
        }
        {
            var Q0;
            Q0=makeQuery(id+"F1.opExtrude","CAP_FACE",FACE,{"disambiguationData":[OSD([sQuery(id+"F0.wireOp",EDGE,"E1")])],"isStart":true});
            var sketch = newSketch(context, id + "F8", { "sketchPlane" : qUnion([Q0])});
            skText(sketch, "E19", { "text": "Jaden\n", "fontName": "RobotoSlab-Bold.ttf"});
            const initialGuessF8  = {"E19": [-0.0408, 0.006, 1, 0, 0.02]};
            skSetInitialGuess(sketch, initialGuessF8);
            skSolve(sketch);
        }
        {
            var Q0;
            Q0=makeQuery(id+"F3.opExtrude","CAP_FACE",FACE,{"disambiguationData":[OSD([sQuery(id+"F2.wireOp",EDGE,"E2.0"),sQuery(id+"F2.wireOp",EDGE,"E3"),sQuery(id+"F2.wireOp",EDGE,"E4"),sQuery(id+"F2.wireOp",EDGE,"E5")])],"isStart":true});
            var sketch = newSketch(context, id + "F9", { "sketchPlane" : qUnion([Q0])});
            skPoint(sketch, "E20", {"position": v(0, 49.3) * mm});
            skSolve(sketch);
        }
        {
            var Q0;
            Q0=sQuery(id+"F9.wireOp",VERTEX,"E20");
            var Q1;
            Q1=makeQuery(id+"F1.opExtrude","SWEPT_BODY",BODY,{"disambiguationData":[OSD([sQuery(id+"F0.wireOp",EDGE,"E1")])]});
            hole(context, id + "F10", {"style" : HoleStyle.SIMPLE, "endStyle" : HoleEndStyle.THROUGH, "holeDiameter" : 6 * mm, "majorDiameter" : 5 * mm, "isTappedThrough" : true, "tappedDepth" : 12 * mm, "tapClearance" : 3, "locations" : qUnion([Q0]), "scope" : qUnion([Q1])});
        }
        {
            var Q0;
            Q0=makeQuery(id+"F8.imprint","IMPRINT",FACE,{"disambiguationData":[TD([[makeQuery(id+"F8.imprint","IMPRINT",EDGE,{"derivedFrom":sQuery(id+"F8.wireOp",EDGE,"E19.sketch_text.stroke-0")}),1.0]])]});
            var sketch = newSketch(context, id + "F11", { "sketchPlane" : qUnion([Q0])});
            skText(sketch, "E21", { "text": "VDB", "fontName": "RobotoSlab-Bold.ttf"});
            const initialGuessF11  = {"E21": [-0.0292, -0.026, 1, 0, 0.02]};
            skSetInitialGuess(sketch, initialGuessF11);
            skSolve(sketch);
        }
        {
            var Q0;
            Q0 = qSketchRegion(id + "F11", true);
            var Q1;
            Q1 = qSketchRegion(id + "F8", true);
            extrude(context, id + "F12", {"entities" : qUnion([Q0, Q1]), "operationType" : NewBodyOperationType.REMOVE, "oppositeDirection" : true, "depth" : 3 * mm, "offsetDistance" : 25 * mm});
        }
        {
            var Q0;
            Q0=makeQuery(id+"F3.opExtrude","CAP_EDGE",EDGE,{"disambiguationData":[OSD([sQuery(id+"F2.wireOp",EDGE,"E3")])],"isStart":true});
            var Q1;
            Q1=makeQuery(id+"F3.opExtrude","CAP_EDGE",EDGE,{"disambiguationData":[OSD([sQuery(id+"F2.wireOp",EDGE,"E3")])],"isStart":false});
            var Q2;
            Q2=makeQuery(id+"F3.opExtrude","CAP_EDGE",EDGE,{"disambiguationData":[OSD([sQuery(id+"F2.wireOp",EDGE,"E4")])],"isStart":false});
            var Q3;
            Q3=makeQuery(id+"F3.opExtrude","CAP_EDGE",EDGE,{"disambiguationData":[OSD([sQuery(id+"F2.wireOp",EDGE,"E4")])],"isStart":true});
            var Q4;
            Q4=makeQuery(id+"F3.opExtrude","SWEPT_EDGE",EDGE,{"disambiguationData":[OSD([sQuery(id+"F2.wireOp",EDGE,"E3"),sQuery(id+"F2.wireOp",EDGE,"E4")])]});
            var Q5;
            Q5=makeQuery(id+"F3.opExtrude","SWEPT_EDGE",EDGE,{"disambiguationData":[OSD([sQuery(id+"F2.wireOp",EDGE,"E4"),sQuery(id+"F2.wireOp",EDGE,"E5")])]});
            var Q6;
            Q6=makeQuery(id+"F3.opExtrude","CAP_EDGE",EDGE,{"disambiguationData":[OSD([sQuery(id+"F2.wireOp",EDGE,"E5")])],"isStart":true});
            var Q7;
            Q7=makeQuery(id+"F3.opExtrude","CAP_EDGE",EDGE,{"disambiguationData":[OSD([sQuery(id+"F2.wireOp",EDGE,"E5")])],"isStart":false});
            fillet(context, id + "F13", {"entities" : qUnion([Q0, Q1, Q2, Q3, Q4, Q5, Q6, Q7]), "radius" : 1.75 * mm, "tangentPropagation" : true, "allowEdgeOverflow" : false});
        }
    });
